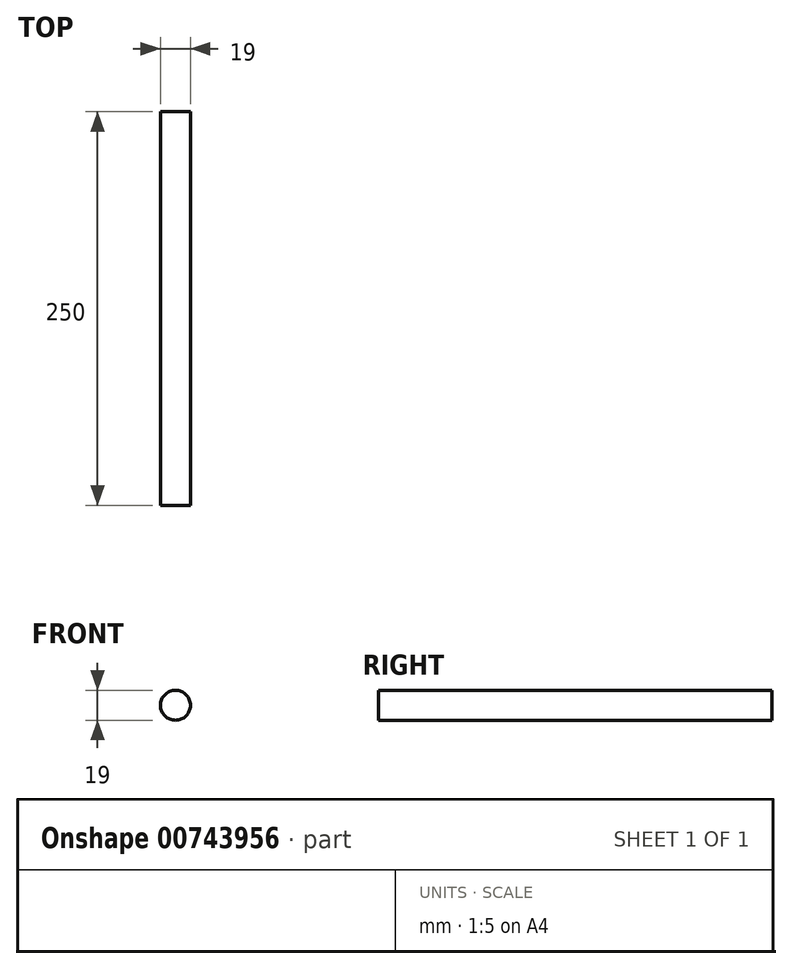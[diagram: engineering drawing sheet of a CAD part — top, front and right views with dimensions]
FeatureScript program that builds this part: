
annotation { "Feature Type Name" : "Feature", "Feature Type Description" : "" }
export const myFeature = defineFeature(function(context is Context, id is Id, definition is map)
    precondition{}
    {
        {
            var Q0;
            Q0=qCreatedBy(makeId("Front.planeOp"),FACE);
            var sketch = newSketch(context, id + "F0", { "sketchPlane" : qUnion([Q0])});
            skCircle(sketch, "E0", {"center": v(0, 0) * mm, "radius": 9.5 * mm});
            skSolve(sketch);
        }
        {
            var Q0;
            Q0=makeQuery(id+"F0.imprint","IMPRINT",FACE,{"disambiguationData":[TD([[makeQuery(id+"F0.imprint","IMPRINT",EDGE,{"derivedFrom":sQuery(id+"F0.wireOp",EDGE,"E0")}),1.0]])]});
            extrude(context, id + "F1", {"entities" : qUnion([Q0]), "depth" : 250 * mm, "offsetDistance" : 25 * mm});
        }
    });
